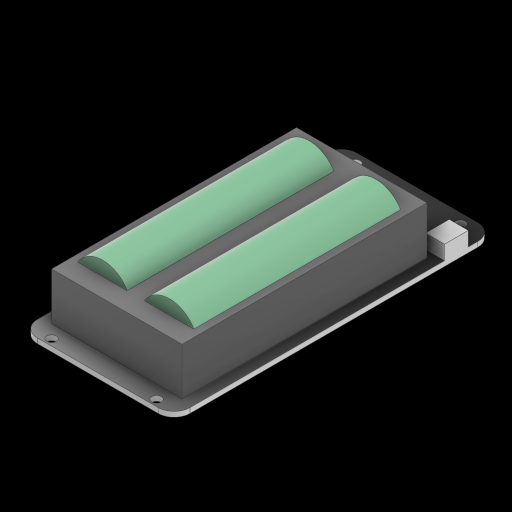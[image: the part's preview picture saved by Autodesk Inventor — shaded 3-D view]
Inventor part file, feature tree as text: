
AUTODESK INVENTOR PART (.ipt)
format: ipt  version: 2024 (Build 280153000, 153)  size: 301,568 bytes
history: native  units: mm
features: sketch x9, extrude x8, fillet x3, projected_geometry x2, hole x1
ambient origin geometry x8: Origin, YZ Plane, XZ Plane, XY Plane, X Axis, Y Axis, Z Axis, Center Point
bodies: Volumenkörper1 (feature_tree)
feature tree (23):
  extrude  "Extrusion1"  Depth=100.5mm
  fillet  "Rundung1"  Radius=1.6mm
  extrude  "Extrusion2"  Depth=32.5mm
  fillet  "Rundung2"  Radius=17.5mm
  extrude  "Extrusion3"  Depth=6.5mm
  fillet  "Rundung3"  Radius=5.0mm
  extrude  "Extrusion4"  Depth=7.5mm
  extrude  "Extrusion5"  Depth=9.0mm
  extrude  "Extrusion6"  Depth=2.0mm
  extrude  "Extrusion7"  Depth=7.5mm
  extrude  "Extrusion8"  Depth=8.0mm
  hole  "Bohrung1"  [1 undecoded]
  sketch  "Skizze1"  dims[d0=48.0mm d1=100.5mm d2=1.6mm d3=0.0mm]
  sketch  "Skizze2"  dims[d4=5.0mm d5=32.5mm d6=17.5mm]
  sketch  "Skizze3"  dims[d7=6.5mm d8=6.5mm d9=5.0mm d10=0.0mm]
  sketch  "Skizze4"  dims[d11=0.5mm d12=7.5mm]
  sketch  "Skizze5"  dims[d13=7.0mm d14=9.0mm]
  sketch  "Skizze6"  dims[d15=5.0mm d16=0.0mm d17=2.0mm]
  sketch  "Skizze7"  dims[d19=8.0mm d20=7.5mm]
  sketch  "Skizze8"  dims[d21=6.0mm d22=8.0mm]
  projected_geometry  "Projizierte Kontur1"
  projected_geometry  "Projizierte Kontur2"
  sketch  "Skizze9"  dims[d23=9.0mm d24=4.5mm d25=2.0mm d26=4.5mm d27=0.0mm d28=1.5mm d29=6.0mm d30=1.0mm d31=2.0mm d32=3.0mm d33=0.0mm d34=6.0mm d35=3.5mm d36=3.5mm d37=77.0mm d38=15.0mm d39=0.0mm d40=18.0mm d41=18.0mm d42=21.0mm d43=21.0mm d44=21.0mm d45=10.5mm d46=77.0mm d47=0.0mm d48=6.0mm d49=6.0mm d50=10.0mm d51=0.0mm d52=33.0mm d53=95.5mm d54=3.0mm d55=0.0mm d56=3.0mm d57=6.0mm d58=18.0mm d59=11.0mm d60=90.0deg d61=8.0mm d62=20.594885mm]
note: 1 required parameter value undecoded (feature->parameter linkage not recoverable at this tier; creation-order binding heuristic only, values carry confidence <= 0.55)
